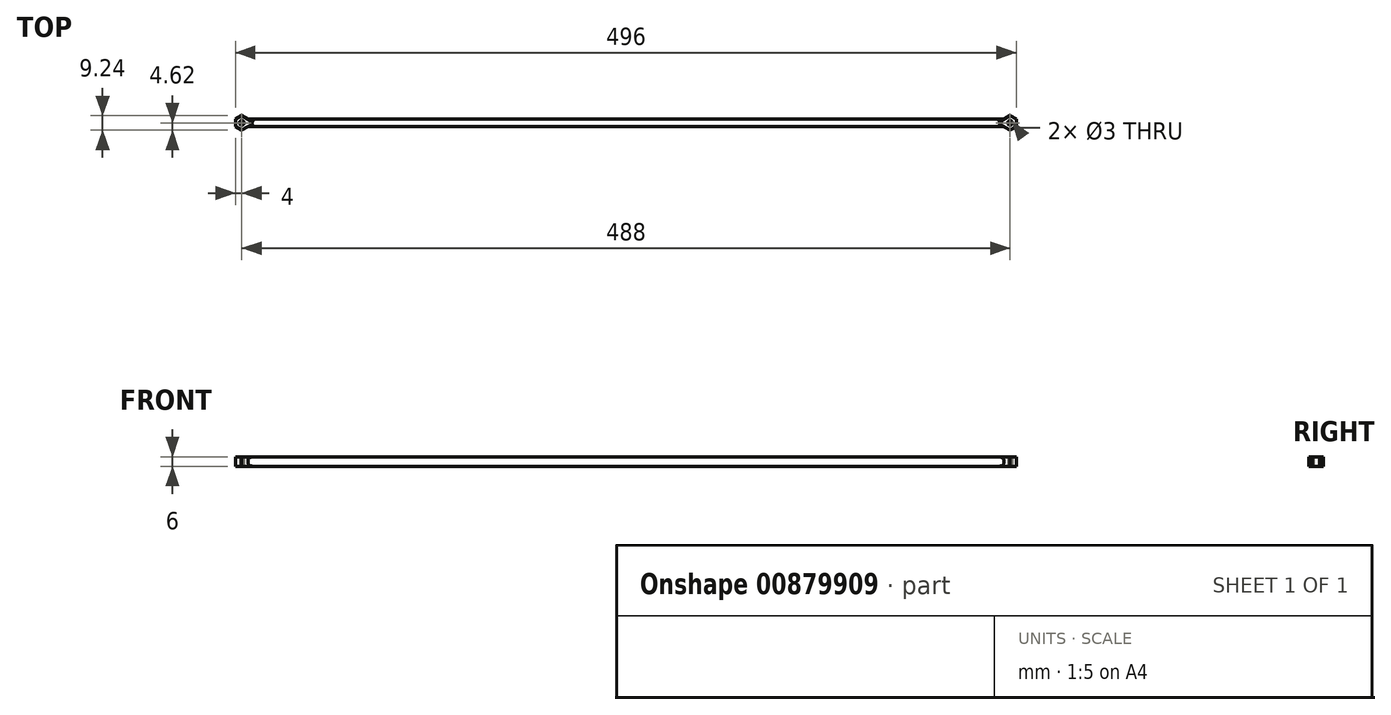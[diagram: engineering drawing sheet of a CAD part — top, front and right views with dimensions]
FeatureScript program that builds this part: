
annotation { "Feature Type Name" : "Feature", "Feature Type Description" : "" }
export const myFeature = defineFeature(function(context is Context, id is Id, definition is map)
    precondition{}
    {
        {
            var Q0;
            Q0=qCreatedBy(makeId("Top.planeOp"),FACE);
            var sketch = newSketch(context, id + "F0", { "sketchPlane" : qUnion([Q0])});
            skCircle(sketch, "E0", {"center": v(0, 0) * mm, "radius": 1.5 * mm});
            skCircle(sketch, "E1.cCircle", {"center": v(0, 0) * mm, "radius": 4 * mm, "construction": true});
            skLineSegment(sketch, "E1.0", {"start": v(-4, -2.3) * mm, "end": v(-4, 2.3) * mm});
            skLineSegment(sketch, "E1.1", {"start": v(-4, 2.3) * mm, "end": v(0, 4.62) * mm});
            skLineSegment(sketch, "E1.2", {"start": v(0, 4.62) * mm, "end": v(4, 2.3) * mm});
            skLineSegment(sketch, "E1.3", {"start": v(4, 2.3) * mm, "end": v(4, -2.3) * mm});
            skLineSegment(sketch, "E1.4", {"start": v(4, -2.3) * mm, "end": v(0, -4.62) * mm});
            skLineSegment(sketch, "E1.5", {"start": v(0, -4.62) * mm, "end": v(-4, -2.3) * mm});
            skPoint(sketch, "E1.0.midPoint", {"position": v(-4, 0) * mm});
            skSolve(sketch);
        }
        {
            var Q0;
            Q0=makeQuery(id+"F0.imprint","IMPRINT",FACE,{"disambiguationData":[TD([[makeQuery(id+"F0.imprint","IMPRINT",EDGE,{"derivedFrom":sQuery(id+"F0.wireOp",EDGE,"E0")}),-1.0]])]});
            extrude(context, id + "F1", {"entities" : qUnion([Q0]), "depth" : 6 * mm, "offsetDistance" : 25 * mm});
        }
        {
            var Q0;
            Q0=makeQuery(id+"F1.opExtrude","SWEPT_FACE",FACE,{"disambiguationData":[OSD([sQuery(id+"F0.wireOp",EDGE,"E1.3")])]});
            extrude(context, id + "F2", {"entities" : qUnion([Q0]), "operationType" : NewBodyOperationType.ADD, "depth" : 240 * mm, "offsetDistance" : 25 * mm});
        }
        {
            var Q0;
            Q0=makeQuery(id+"F1.opExtrude","SWEPT_BODY",BODY,{"disambiguationData":[OSD([sQuery(id+"F0.wireOp",EDGE,"E0"),sQuery(id+"F0.wireOp",EDGE,"E1.0"),sQuery(id+"F0.wireOp",EDGE,"E1.1"),sQuery(id+"F0.wireOp",EDGE,"E1.2"),sQuery(id+"F0.wireOp",EDGE,"E1.3"),sQuery(id+"F0.wireOp",EDGE,"E1.4"),sQuery(id+"F0.wireOp",EDGE,"E1.5")])]});
            var Q1;
            Q1=makeQuery(id+"F2.opExtrude","CAP_FACE",FACE,{"disambiguationData":[OSD([sQuery(id+"F0.wireOp",EDGE,"E1.3")])],"isStart":false});
            mirror(context, id + "F3", {"operationType" : NewBodyOperationType.ADD, "entities" : qUnion([Q0]), "mirrorPlane" : qUnion([Q1])});
        }
        {
            var Q0;
            {var subQ0=sQuery(id+"F0.wireOp",EDGE,"E1.4");var subQ1=sQuery(id+"F0.wireOp",EDGE,"E1.3");var subQ2=makeQuery(id+"F2.opExtrude","SWEPT_EDGE",EDGE,{"disambiguationData":[OSD([subQ1,subQ0]),TDD([makeQuery(id+"F1.opExtrude","CAP_VERTEX",VERTEX,{"disambiguationData":[OSD([subQ1,subQ0])],"isStart":false})])]});Q0=makeQuery(id+"F3.boolean.opBoolean","MERGE",EDGE,{"derivedFrom":[subQ2,makeQuery(id+"F3.opPattern","COPY",EDGE,{"derivedFrom":subQ2,"instanceName":"1"})]});}
            var Q1;
            {var subQ0=sQuery(id+"F0.wireOp",EDGE,"E1.3");var subQ1=sQuery(id+"F0.wireOp",EDGE,"E1.2");var subQ2=makeQuery(id+"F2.opExtrude","SWEPT_EDGE",EDGE,{"disambiguationData":[OSD([subQ1,subQ0]),TDD([makeQuery(id+"F1.opExtrude","CAP_VERTEX",VERTEX,{"disambiguationData":[OSD([subQ1,subQ0])],"isStart":false})])]});Q1=makeQuery(id+"F3.boolean.opBoolean","MERGE",EDGE,{"derivedFrom":[subQ2,makeQuery(id+"F3.opPattern","COPY",EDGE,{"derivedFrom":subQ2,"instanceName":"1"})]});}
            var Q2;
            {var subQ0=sQuery(id+"F0.wireOp",EDGE,"E1.4");var subQ1=sQuery(id+"F0.wireOp",EDGE,"E1.3");var subQ2=makeQuery(id+"F2.opExtrude","SWEPT_EDGE",EDGE,{"disambiguationData":[OSD([subQ1,subQ0]),TDD([makeQuery(id+"F1.opExtrude","CAP_VERTEX",VERTEX,{"disambiguationData":[OSD([subQ1,subQ0])],"isStart":true})])]});Q2=makeQuery(id+"F3.boolean.opBoolean","MERGE",EDGE,{"derivedFrom":[subQ2,makeQuery(id+"F3.opPattern","COPY",EDGE,{"derivedFrom":subQ2,"instanceName":"1"})]});}
            var Q3;
            {var subQ0=sQuery(id+"F0.wireOp",EDGE,"E1.3");var subQ1=sQuery(id+"F0.wireOp",EDGE,"E1.2");var subQ2=makeQuery(id+"F2.opExtrude","SWEPT_EDGE",EDGE,{"disambiguationData":[OSD([subQ1,subQ0]),TDD([makeQuery(id+"F1.opExtrude","CAP_VERTEX",VERTEX,{"disambiguationData":[OSD([subQ1,subQ0])],"isStart":true})])]});Q3=makeQuery(id+"F3.boolean.opBoolean","MERGE",EDGE,{"derivedFrom":[subQ2,makeQuery(id+"F3.opPattern","COPY",EDGE,{"derivedFrom":subQ2,"instanceName":"1"})]});}
            fillet(context, id + "F4", {"entities" : qUnion([Q0, Q1, Q2, Q3]), "radius" : 2 * mm, "tangentPropagation" : true, "allowEdgeOverflow" : false});
        }
    });
